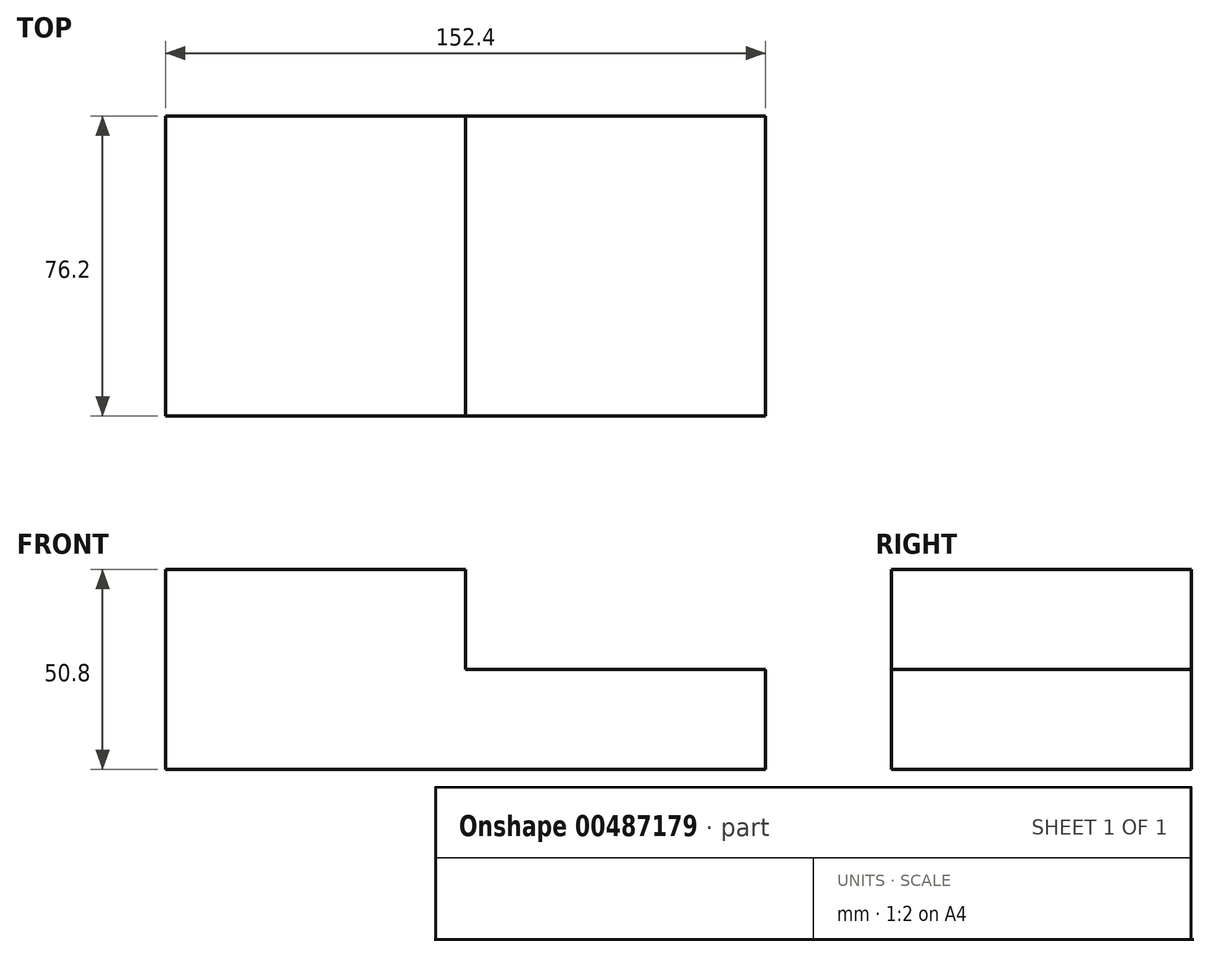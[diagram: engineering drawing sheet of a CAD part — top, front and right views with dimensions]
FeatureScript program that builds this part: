
annotation { "Feature Type Name" : "Feature", "Feature Type Description" : "" }
export const myFeature = defineFeature(function(context is Context, id is Id, definition is map)
    precondition{}
    {
        {
            var Q0;
            Q0=qCreatedBy(makeId("Front.planeOp"),FACE);
            var sketch = newSketch(context, id + "F0", { "sketchPlane" : qUnion([Q0])});
            skLineSegment(sketch, "E0", {"start": v(-100.33, 61.05) * mm, "end": v(-24.13, 61.05) * mm});
            skLineSegment(sketch, "E1", {"start": v(-24.13, 61.05) * mm, "end": v(-24.13, 35.65) * mm});
            skLineSegment(sketch, "E2", {"start": v(-24.13, 35.65) * mm, "end": v(52.07, 35.65) * mm});
            skLineSegment(sketch, "E3", {"start": v(52.07, 35.65) * mm, "end": v(52.07, 10.25) * mm});
            skLineSegment(sketch, "E4", {"start": v(52.07, 10.25) * mm, "end": v(-100.33, 10.25) * mm});
            skLineSegment(sketch, "E5", {"start": v(-100.33, 10.25) * mm, "end": v(-100.33, 61.05) * mm});
            skSolve(sketch);
        }
        {
            var Q0;
            Q0 = qSketchRegion(id + "F0", true);
            extrude(context, id + "F1", {"entities" : qUnion([Q0]), "depth" : 76.2 * mm});
        }
    });
